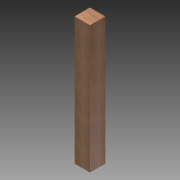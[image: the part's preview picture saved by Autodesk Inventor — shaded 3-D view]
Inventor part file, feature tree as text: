
AUTODESK INVENTOR PART (.ipt)
format: ipt  version: 2015 (Build 190159000, 159)  size: 86,528 bytes
history: native  units: in
note: dims shown in document units (in); Inventor stores cm internally (conversion verified against a paired STEP export)
features: other x2, extrude x1, sketch x1
ambient origin geometry x8: Origin, YZ Plane, XZ Plane, XY Plane, X Axis, Y Axis, Z Axis, Center Point
bodies: Solid1 (feature_tree)
feature tree (4):
  extrude  "Extrusion1"  Depth=50.0in TaperAngle=0.0deg
  other  "Work Axis1"
  sketch  "Sketch1"  dims[d0=6.0in d1=50.0in d2=0.0in]
  other  "Work Point1"
